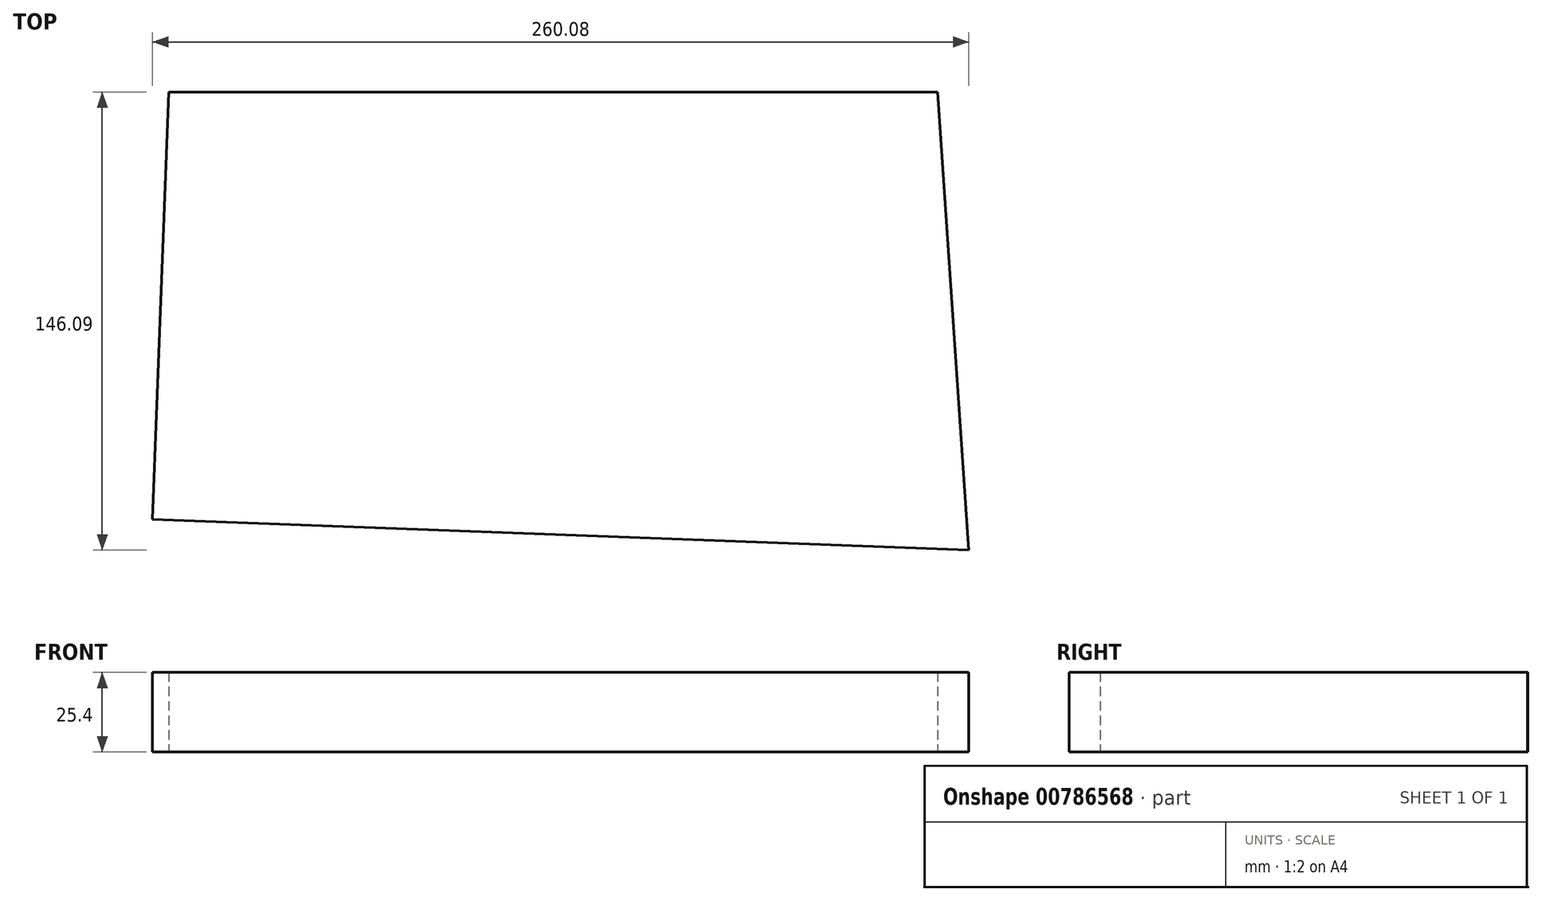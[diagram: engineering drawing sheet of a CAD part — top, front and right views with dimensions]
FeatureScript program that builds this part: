
annotation { "Feature Type Name" : "Feature", "Feature Type Description" : "" }
export const myFeature = defineFeature(function(context is Context, id is Id, definition is map)
    precondition{}
    {
        {
            var Q0;
            Q0=qCreatedBy(makeId("Top.planeOp"),FACE);
            var sketch = newSketch(context, id + "F0", { "sketchPlane" : qUnion([Q0])});
            skLineSegment(sketch, "E0", {"start": v(-125.62, 73.45) * mm, "end": v(-130.76, -62.82) * mm});
            skLineSegment(sketch, "E1", {"start": v(-130.76, -62.82) * mm, "end": v(129.32, -72.64) * mm});
            skLineSegment(sketch, "E2", {"start": v(129.32, -72.64) * mm, "end": v(119.34, 73.4) * mm});
            skLineSegment(sketch, "E3", {"start": v(119.34, 73.4) * mm, "end": v(-125.62, 73.45) * mm});
            skSolve(sketch);
        }
        {
            var Q0;
            Q0=makeQuery(id+"F0.imprint","IMPRINT",FACE,{"disambiguationData":[TD([[makeQuery(id+"F0.imprint","IMPRINT",EDGE,{"derivedFrom":sQuery(id+"F0.wireOp",EDGE,"E0")}),1.0]])]});
            extrude(context, id + "F1", {"entities" : qUnion([Q0]), "depth" : 25.4 * mm, "offsetDistance" : 25.4 * mm});
        }
    });
